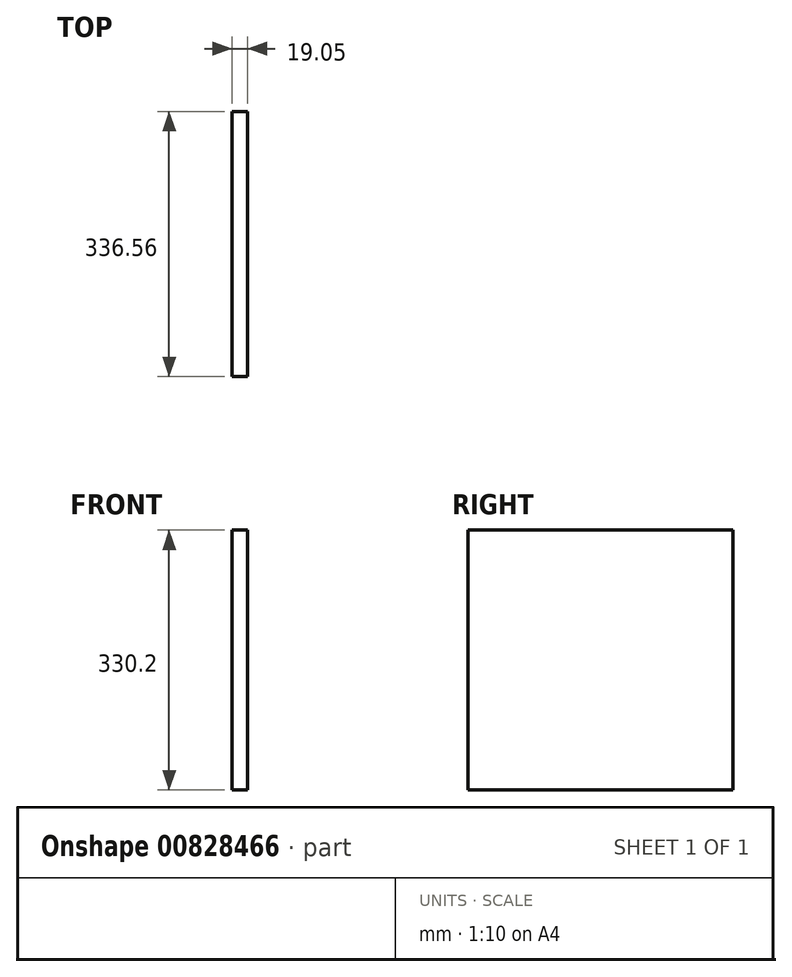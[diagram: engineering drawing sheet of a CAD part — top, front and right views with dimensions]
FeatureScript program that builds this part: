
annotation { "Feature Type Name" : "Feature", "Feature Type Description" : "" }
export const myFeature = defineFeature(function(context is Context, id is Id, definition is map)
    precondition{}
    {
        {
            var Q0;
            Q0=qCreatedBy(makeId("Right.planeOp"),FACE);
            var sketch = newSketch(context, id + "F0", { "sketchPlane" : qUnion([Q0])});
            skLineSegment(sketch, "E0.bottom", {"start": v(168.27, 165.1) * mm, "end": v(-168.28, 165.1) * mm});
            skLineSegment(sketch, "E0.top", {"start": v(168.27, -165.1) * mm, "end": v(-168.28, -165.1) * mm});
            skLineSegment(sketch, "E0.left", {"start": v(168.28, 165.1) * mm, "end": v(168.27, -165.1) * mm});
            skLineSegment(sketch, "E0.right", {"start": v(-168.28, 165.1) * mm, "end": v(-168.28, -165.1) * mm});
            skPoint(sketch, "E0.middle", {"position": v(0, 0) * mm});
            skSolve(sketch);
        }
        {
            var Q0;
            Q0=makeQuery(id+"F0.imprint","IMPRINT",FACE,{"disambiguationData":[TD([[makeQuery(id+"F0.imprint","IMPRINT",EDGE,{"derivedFrom":sQuery(id+"F0.wireOp",EDGE,"E0.bottom")}),1.0]])]});
            extrude(context, id + "F1", {"entities" : qUnion([Q0]), "depth" : 19.05 * mm, "offsetDistance" : 25.4 * mm});
        }
    });
